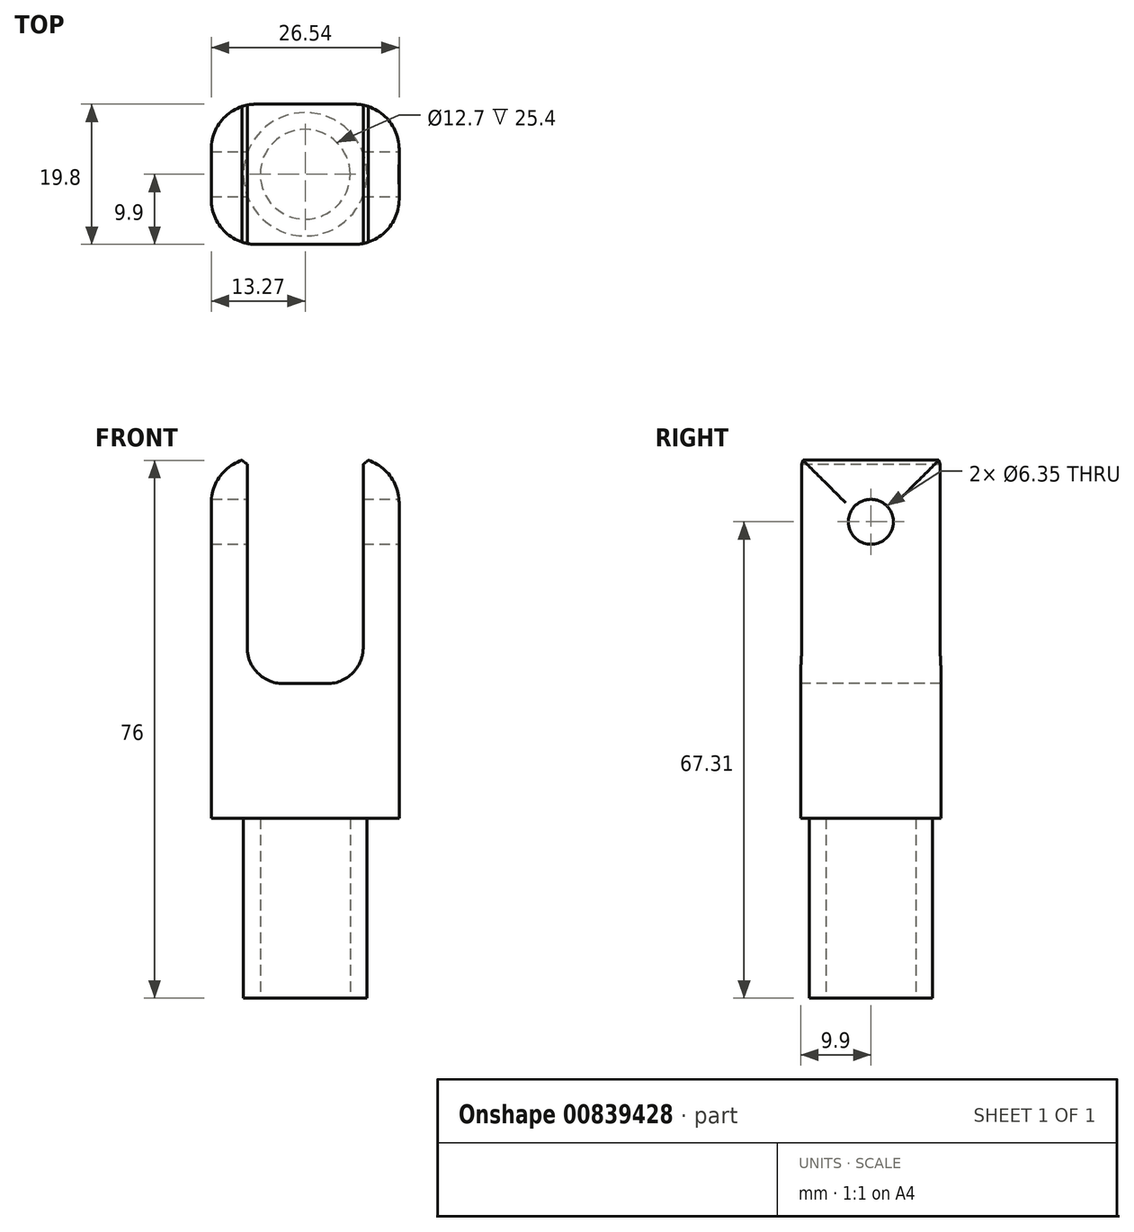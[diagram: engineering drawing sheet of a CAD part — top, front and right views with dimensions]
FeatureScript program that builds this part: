
annotation { "Feature Type Name" : "Feature", "Feature Type Description" : "" }
export const myFeature = defineFeature(function(context is Context, id is Id, definition is map)
    precondition{}
    {
        {
            var Q0;
            Q0=qCreatedBy(makeId("Top.planeOp"),FACE);
            var sketch = newSketch(context, id + "F0", { "sketchPlane" : qUnion([Q0])});
            skCircle(sketch, "E0", {"center": v(0, 0) * mm, "radius": 8.72 * mm});
            skSolve(sketch);
        }
        {
            var Q0;
            Q0=qSketchRegion(id+"F0",true);
            extrude(context, id + "F1", {"entities" : qUnion([Q0]), "depth" : 25.4 * mm, "offsetDistance" : 25.4 * mm});
        }
        {
            var Q0;
            Q0=makeQuery(id+"F1.opExtrude","CAP_FACE",FACE,{"disambiguationData":[OSD([sQuery(id+"F0.wireOp",EDGE,"E0")])],"isStart":false});
            var sketch = newSketch(context, id + "F2", { "sketchPlane" : qUnion([Q0])});
            skCircle(sketch, "E1", {"center": v(0, 0) * mm, "radius": 19.05 * mm});
            skSolve(sketch);
        }
        {
            var Q0;
            Q0=qSketchRegion(id+"F2",true);
            extrude(context, id + "F3", {"entities" : qUnion([Q0]), "operationType" : NewBodyOperationType.ADD, "depth" : 50.8 * mm, "offsetDistance" : 25.4 * mm});
        }
        {
            var Q0;
            Q0=qCreatedBy(makeId("Front.planeOp"),FACE);
            var sketch = newSketch(context, id + "F4", { "sketchPlane" : qUnion([Q0])});
            skLineSegment(sketch, "E2.bottom", {"start": v(8.2, 82.55) * mm, "end": v(-8.2, 82.55) * mm});
            skLineSegment(sketch, "E2.top", {"start": v(8.2, 44.45) * mm, "end": v(-8.2, 44.45) * mm});
            skLineSegment(sketch, "E2.left", {"start": v(8.2, 82.55) * mm, "end": v(8.2, 44.45) * mm});
            skLineSegment(sketch, "E2.right", {"start": v(-8.2, 82.55) * mm, "end": v(-8.2, 44.45) * mm});
            skPoint(sketch, "E2.middle", {"position": v(0, 63.5) * mm});
            skLineSegment(sketch, "E3.bottom", {"start": v(-22.78, 79.6) * mm, "end": v(-13.27, 79.6) * mm});
            skLineSegment(sketch, "E3.top", {"start": v(-22.78, 19.68) * mm, "end": v(-13.27, 19.68) * mm});
            skLineSegment(sketch, "E3.left", {"start": v(-22.78, 79.6) * mm, "end": v(-22.78, 19.68) * mm});
            skLineSegment(sketch, "E3.right", {"start": v(-13.27, 79.6) * mm, "end": v(-13.27, 19.68) * mm});
            skLineSegment(sketch, "E4.MirrorCS", {"start": v(13.27, 79.6) * mm, "end": v(13.27, 19.68) * mm});
            skLineSegment(sketch, "E5.MirrorCS", {"start": v(22.78, 79.6) * mm, "end": v(13.27, 79.6) * mm});
            skLineSegment(sketch, "E6.MirrorCS", {"start": v(22.78, 79.6) * mm, "end": v(22.78, 19.68) * mm});
            skLineSegment(sketch, "E7.MirrorCS", {"start": v(22.78, 19.68) * mm, "end": v(13.27, 19.68) * mm});
            skSolve(sketch);
        }
        {
            var Q0;
            Q0=qSketchRegion(id+"F4",true);
            extrude(context, id + "F5", {"entities" : qUnion([Q0]), "operationType" : NewBodyOperationType.REMOVE, "oppositeDirection" : true, "depth" : 25.4 * mm, "offsetDistance" : 25.4 * mm, "hasSecondDirection" : true, "secondDirectionOppositeDirection" : false, "secondDirectionDepth" : 25.4 * mm});
        }
        {
            var Q0;
            Q0=qCreatedBy(makeId("Right.planeOp"),FACE);
            var sketch = newSketch(context, id + "F6", { "sketchPlane" : qUnion([Q0])});
            skCircle(sketch, "E8", {"center": v(0, 67.31) * mm, "radius": 3.18 * mm});
            skSolve(sketch);
        }
        {
            var Q0;
            Q0=qSketchRegion(id+"F6",true);
            extrude(context, id + "F7", {"entities" : qUnion([Q0]), "operationType" : NewBodyOperationType.REMOVE, "oppositeDirection" : true, "depth" : 25.4 * mm, "offsetDistance" : 25.4 * mm, "hasSecondDirection" : true, "secondDirectionOppositeDirection" : false, "secondDirectionDepth" : 25.4 * mm});
        }
        {
            var Q0;
            Q0=makeQuery(id+"F1.opExtrude","CAP_FACE",FACE,{"disambiguationData":[OSD([sQuery(id+"F0.wireOp",EDGE,"E0")])],"isStart":true});
            var sketch = newSketch(context, id + "F8", { "sketchPlane" : qUnion([Q0])});
            skCircle(sketch, "E9", {"center": v(0, 0) * mm, "radius": 6.35 * mm});
            skSolve(sketch);
        }
        {
            var Q0;
            Q0=qSketchRegion(id+"F8",true);
            extrude(context, id + "F9", {"entities" : qUnion([Q0]), "operationType" : NewBodyOperationType.REMOVE, "oppositeDirection" : true, "depth" : 25.4 * mm, "offsetDistance" : 25.4 * mm});
        }
        {
            var Q0;
            Q0=makeQuery(id+"F5.boolean.opBoolean","COPY",EDGE,{"derivedFrom":makeQuery(id+"F5.opExtrude","SWEPT_EDGE",EDGE,{"disambiguationData":[OSD([sQuery(id+"F4.wireOp",EDGE,"E2.top"),sQuery(id+"F4.wireOp",EDGE,"E2.right")])]})});
            var Q1;
            Q1=makeQuery(id+"F5.boolean.opBoolean","COPY",EDGE,{"derivedFrom":makeQuery(id+"F5.opExtrude","SWEPT_EDGE",EDGE,{"disambiguationData":[OSD([sQuery(id+"F4.wireOp",EDGE,"E2.top"),sQuery(id+"F4.wireOp",EDGE,"E2.left")])]})});
            fillet(context, id + "F10", {"entities" : qUnion([Q0, Q1]), "tangentPropagation" : true, "radius" : 5.08 * mm, "defaultsChanged" : false, "vertexSettings" : [], "allowEdgeOverflow" : false});
        }
        {
            var Q0;
            Q0=qCreatedBy(makeId("Right.planeOp"),FACE);
            var sketch = newSketch(context, id + "F11", { "sketchPlane" : qUnion([Q0])});
            skLineSegment(sketch, "E10.bottom", {"start": v(-39.1, 82.2) * mm, "end": v(-9.9, 82.2) * mm});
            skLineSegment(sketch, "E10.top", {"start": v(-39.1, 12.47) * mm, "end": v(-9.9, 12.47) * mm});
            skLineSegment(sketch, "E10.left", {"start": v(-39.1, 82.2) * mm, "end": v(-39.1, 12.47) * mm});
            skLineSegment(sketch, "E10.right", {"start": v(-9.9, 82.2) * mm, "end": v(-9.9, 12.47) * mm});
            skLineSegment(sketch, "E11.MirrorCS", {"start": v(9.9, 82.2) * mm, "end": v(9.9, 12.47) * mm});
            skLineSegment(sketch, "E12.MirrorCS", {"start": v(39.1, 82.2) * mm, "end": v(9.9, 82.2) * mm});
            skLineSegment(sketch, "E13.MirrorCS", {"start": v(39.1, 82.2) * mm, "end": v(39.1, 12.47) * mm});
            skLineSegment(sketch, "E14.MirrorCS", {"start": v(39.1, 12.47) * mm, "end": v(9.9, 12.47) * mm});
            skSolve(sketch);
        }
        {
            var Q0;
            Q0 = qSketchRegion(id + "F11", true);
            extrude(context, id + "F12", {"entities" : qUnion([Q0]), "operationType" : NewBodyOperationType.REMOVE, "endBound" : BoundingType.THROUGH_ALL, "oppositeDirection" : true, "depth" : 25.4 * mm, "offsetDistance" : 25.4 * mm, "hasSecondDirection" : true, "secondDirectionBound" : BoundingType.THROUGH_ALL, "secondDirectionOppositeDirection" : false, "secondDirectionDepth" : 25.4 * mm});
        }
        {
            var Q0;
            Q0=makeQuery(id+"F12.boolean.opBoolean","INTERSECT",EDGE,{"derivedFrom":[makeQuery(id+"F5.boolean.opBoolean","COPY",FACE,{"derivedFrom":makeQuery(id+"F5.opExtrude","SWEPT_FACE",FACE,{"disambiguationData":[OSD([sQuery(id+"F4.wireOp",EDGE,"E3.right")])]})}),makeQuery(id+"F12.opExtrude","SWEPT_FACE",FACE,{"disambiguationData":[OSD([sQuery(id+"F11.wireOp",EDGE,"E10.right")])]})]});
            var Q1;
            Q1=makeQuery(id+"F12.boolean.opBoolean","INTERSECT",EDGE,{"derivedFrom":[makeQuery(id+"F5.boolean.opBoolean","COPY",FACE,{"derivedFrom":makeQuery(id+"F5.opExtrude","SWEPT_FACE",FACE,{"disambiguationData":[OSD([sQuery(id+"F4.wireOp",EDGE,"E4.MirrorCS")])]})}),makeQuery(id+"F12.opExtrude","SWEPT_FACE",FACE,{"disambiguationData":[OSD([sQuery(id+"F11.wireOp",EDGE,"E10.right")])]})]});
            var Q2;
            Q2=makeQuery(id+"F12.boolean.opBoolean","INTERSECT",EDGE,{"derivedFrom":[makeQuery(id+"F5.boolean.opBoolean","COPY",FACE,{"derivedFrom":makeQuery(id+"F5.opExtrude","SWEPT_FACE",FACE,{"disambiguationData":[OSD([sQuery(id+"F4.wireOp",EDGE,"E4.MirrorCS")])]})}),makeQuery(id+"F12.opExtrude","SWEPT_FACE",FACE,{"disambiguationData":[OSD([sQuery(id+"F11.wireOp",EDGE,"E11.MirrorCS")])]})]});
            var Q3;
            Q3=makeQuery(id+"F12.boolean.opBoolean","INTERSECT",EDGE,{"derivedFrom":[makeQuery(id+"F5.boolean.opBoolean","COPY",FACE,{"derivedFrom":makeQuery(id+"F5.opExtrude","SWEPT_FACE",FACE,{"disambiguationData":[OSD([sQuery(id+"F4.wireOp",EDGE,"E3.right")])]})}),makeQuery(id+"F12.opExtrude","SWEPT_FACE",FACE,{"disambiguationData":[OSD([sQuery(id+"F11.wireOp",EDGE,"E11.MirrorCS")])]})]});
            var Q4;
            Q4=makeQuery(id+"F5.boolean.opBoolean","INTERSECT",EDGE,{"derivedFrom":[makeQuery(id+"F3.opExtrude","CAP_FACE",FACE,{"disambiguationData":[OSD([sQuery(id+"F2.wireOp",EDGE,"E1")])],"isStart":false}),makeQuery(id+"F5.opExtrude","SWEPT_FACE",FACE,{"disambiguationData":[OSD([sQuery(id+"F4.wireOp",EDGE,"E3.right")])]})]});
            var Q5;
            Q5=makeQuery(id+"F5.boolean.opBoolean","INTERSECT",EDGE,{"derivedFrom":[makeQuery(id+"F3.opExtrude","CAP_FACE",FACE,{"disambiguationData":[OSD([sQuery(id+"F2.wireOp",EDGE,"E1")])],"isStart":false}),makeQuery(id+"F5.opExtrude","SWEPT_FACE",FACE,{"disambiguationData":[OSD([sQuery(id+"F4.wireOp",EDGE,"E4.MirrorCS")])]})]});
            fillet(context, id + "F13", {"entities" : qUnion([Q0, Q1, Q2, Q3, Q4, Q5]), "tangentPropagation" : true, "radius" : 6.35 * mm, "defaultsChanged" : false, "vertexSettings" : [], "allowEdgeOverflow" : false});
        }
        {
            var Q0;
            Q0=makeQuery(id+"F13.opFillet","BLEND_EDGE",EDGE,{"blendedFrom":[makeQuery(id+"F5.boolean.opBoolean","INTERSECT",EDGE,{"derivedFrom":[makeQuery(id+"F3.opExtrude","CAP_FACE",FACE,{"disambiguationData":[OSD([sQuery(id+"F2.wireOp",EDGE,"E1")])],"isStart":false}),makeQuery(id+"F5.opExtrude","SWEPT_FACE",FACE,{"disambiguationData":[OSD([sQuery(id+"F4.wireOp",EDGE,"E3.right")])]})]}),makeQuery(id+"F5.boolean.opBoolean","COPY",FACE,{"derivedFrom":makeQuery(id+"F5.opExtrude","SWEPT_FACE",FACE,{"disambiguationData":[OSD([sQuery(id+"F4.wireOp",EDGE,"E2.right")])]})})],"blendedInto":[makeQuery(id+"F5.boolean.opBoolean","COPY",FACE,{"derivedFrom":makeQuery(id+"F5.opExtrude","SWEPT_FACE",FACE,{"disambiguationData":[OSD([sQuery(id+"F4.wireOp",EDGE,"E2.right")])]})})]});
            var Q1;
            Q1=makeQuery(id+"F13.opFillet","BLEND_EDGE",EDGE,{"blendedFrom":[makeQuery(id+"F5.boolean.opBoolean","INTERSECT",EDGE,{"derivedFrom":[makeQuery(id+"F3.opExtrude","CAP_FACE",FACE,{"disambiguationData":[OSD([sQuery(id+"F2.wireOp",EDGE,"E1")])],"isStart":false}),makeQuery(id+"F5.opExtrude","SWEPT_FACE",FACE,{"disambiguationData":[OSD([sQuery(id+"F4.wireOp",EDGE,"E4.MirrorCS")])]})]}),makeQuery(id+"F5.boolean.opBoolean","COPY",FACE,{"derivedFrom":makeQuery(id+"F5.opExtrude","SWEPT_FACE",FACE,{"disambiguationData":[OSD([sQuery(id+"F4.wireOp",EDGE,"E2.left")])]})})],"blendedInto":[makeQuery(id+"F5.boolean.opBoolean","COPY",FACE,{"derivedFrom":makeQuery(id+"F5.opExtrude","SWEPT_FACE",FACE,{"disambiguationData":[OSD([sQuery(id+"F4.wireOp",EDGE,"E2.left")])]})})]});
            chamfer(context, id + "F14", {"entities" : qUnion([Q0, Q1]), "width" : 0.76 * mm, "tangentPropagation" : true});
        }
    });
